# Revit family: Shower-Haws_Corporation-Drench_Shower_8122
name_source: partatom
category: Plumbing Fixtures
revit_build: Autodesk Revit MEP 2013 (Build: 20130531_2115(x64)
units: mm (PartAtom-declared; Revit-internal decimal feet)

## types (1)
- 8122
    Assembly Code = D2010710
    CW Connection = Yes
    CWFU = 1
    Connection Radius = 1/2"
    Cost Note = For Cost information please visit the Resource tab in the Product Page URL
    Description = Requires minimal maintenance and is equipped with test card to record weekly testing
    Flow = 31 GPM
    HW Connection = No
    HWFU = 1
    Head Level = 86 1/4"
    Keynote = 15410
    Manufacturer = Haws Corporation 1455 Kleppe Lane Sparks, NV 89431
    Max.Overhang = 16 1/4"
    Model = 8122
    Product Documentation Link = http://www.hawsco.com
    Product Page URL = http://www.hawsco.com
    Pull Rod = Metal - Haws Corporation - High Polished Stainless Steel
    Pull Rod Height = 69"
    Series = AXION MSR™
    Shower Head = Metal - Haws Corporation - Green Powder Coating
    Supply Radius = 1"
    Tubing = Metal - Haws Corporation - Galvanized Steel
    Type Comments = Drench shower offers a new hydrodynamic shower design that minimizes the strong physical pressure
    URL = http://www.hawsco.com
    Vent Connection = No
    WFU = 1
    Waste Connection = Yes

## geometry (parser evidence)
native form markers: Blend x31, Sweep x7
no freeform markers — native parametric forms only
